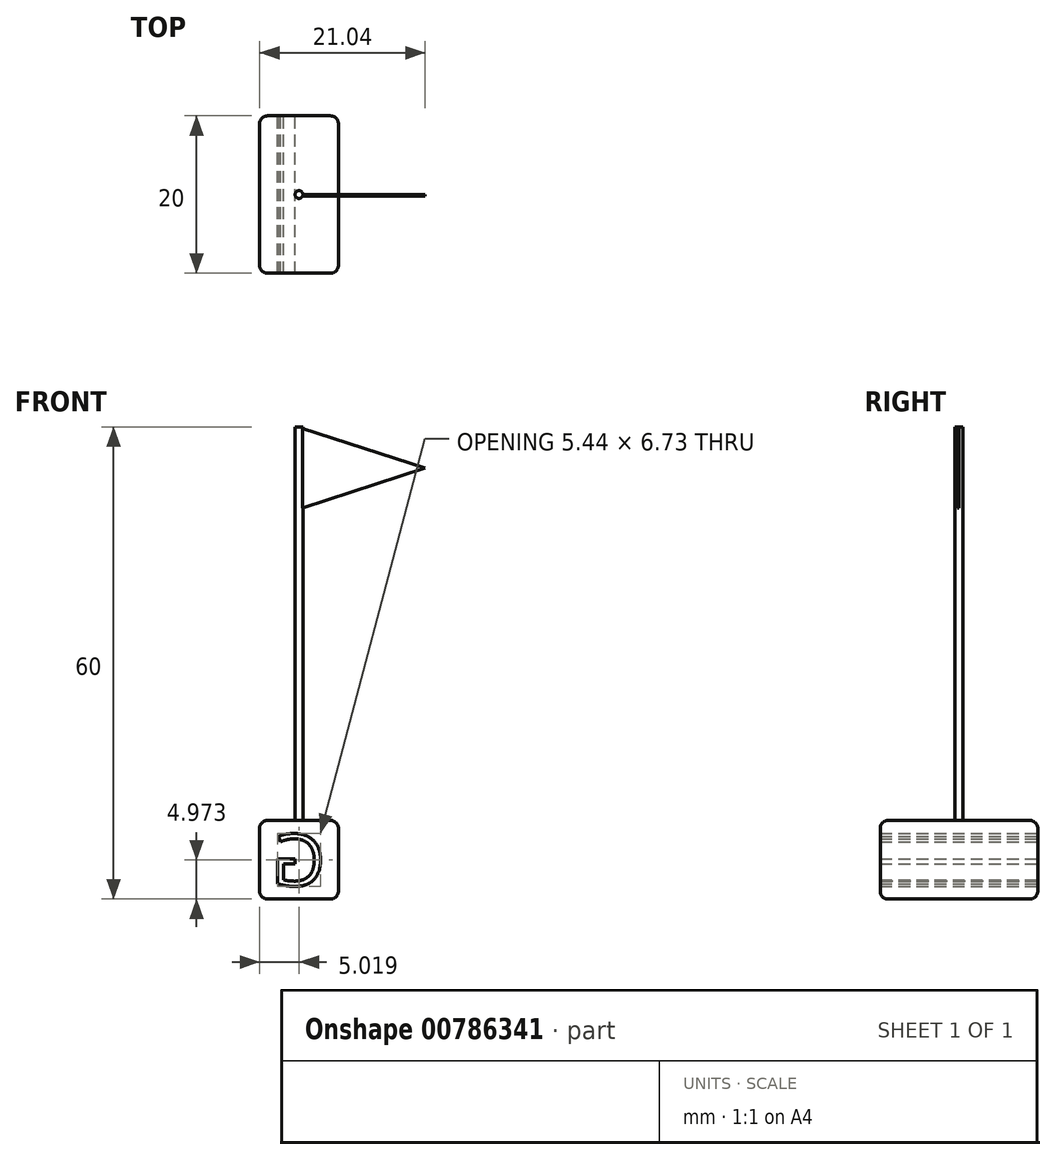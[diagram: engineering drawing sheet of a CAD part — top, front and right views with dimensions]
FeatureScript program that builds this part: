
annotation { "Feature Type Name" : "Feature", "Feature Type Description" : "" }
export const myFeature = defineFeature(function(context is Context, id is Id, definition is map)
    precondition{}
    {
        {
            var Q0;
            Q0=qCreatedBy(makeId("Front.planeOp"),FACE);
            var sketch = newSketch(context, id + "F0", { "sketchPlane" : qUnion([Q0])});
            skLineSegment(sketch, "E0.bottom", {"start": v(0, 0) * mm, "end": v(10, 0) * mm});
            skLineSegment(sketch, "E0.top", {"start": v(0, 10) * mm, "end": v(10, 10) * mm});
            skLineSegment(sketch, "E0.left", {"start": v(0, 0) * mm, "end": v(0, 10) * mm});
            skLineSegment(sketch, "E0.right", {"start": v(10, 0) * mm, "end": v(10, 10) * mm});
            skSolve(sketch);
        }
        {
            var Q0;
            Q0 = qSketchRegion(id + "F0", true);
            extrude(context, id + "F1", {"entities" : qUnion([Q0]), "depth" : 20 * mm, "offsetDistance" : 25 * mm});
        }
        {
            var Q0;
            Q0=makeQuery(id+"F1.opExtrude","CAP_FACE",FACE,{"disambiguationData":[OSD([sQuery(id+"F0.wireOp",EDGE,"E0.bottom"),sQuery(id+"F0.wireOp",EDGE,"E0.top"),sQuery(id+"F0.wireOp",EDGE,"E0.left"),sQuery(id+"F0.wireOp",EDGE,"E0.right")])],"isStart":false});
            var Q1;
            Q1=makeQuery(id+"F1.opExtrude","SWEPT_FACE",FACE,{"disambiguationData":[OSD([sQuery(id+"F0.wireOp",EDGE,"E0.right")])]});
            var Q2;
            Q2=makeQuery(id+"F1.opExtrude","CAP_FACE",FACE,{"disambiguationData":[OSD([sQuery(id+"F0.wireOp",EDGE,"E0.bottom"),sQuery(id+"F0.wireOp",EDGE,"E0.top"),sQuery(id+"F0.wireOp",EDGE,"E0.left"),sQuery(id+"F0.wireOp",EDGE,"E0.right")])],"isStart":true});
            var Q3;
            Q3=makeQuery(id+"F1.opExtrude","SWEPT_FACE",FACE,{"disambiguationData":[OSD([sQuery(id+"F0.wireOp",EDGE,"E0.left")])]});
            fillet(context, id + "F2", {"entities" : qUnion([Q0, Q1, Q2, Q3]), "radius" : 1 * mm, "tangentPropagation" : true, "allowEdgeOverflow" : false});
        }
        {
            var Q0;
            Q0=makeQuery(id+"F1.opExtrude","SWEPT_FACE",FACE,{"disambiguationData":[OSD([sQuery(id+"F0.wireOp",EDGE,"E0.top")])]});
            var sketch = newSketch(context, id + "F3", { "sketchPlane" : qUnion([Q0])});
            skLineSegment(sketch, "E1", {"start": v(5, -1) * mm, "end": v(5, -19) * mm, "construction": true});
            skCircle(sketch, "E2", {"center": v(5, -10) * mm, "radius": 0.5 * mm});
            skSolve(sketch);
        }
        {
            var Q0;
            Q0 = qSketchRegion(id + "F3", true);
            extrude(context, id + "F4", {"entities" : qUnion([Q0]), "operationType" : NewBodyOperationType.ADD, "depth" : 50 * mm, "offsetDistance" : 25 * mm});
        }
        {
            var Q0;
            Q0=qCreatedBy(makeId("Front.planeOp"),FACE);
            cPlane(context, id + "F5", {"entities" : qUnion([Q0]), "cplaneType" : CPlaneType.OFFSET, "offset" : 10 * mm, "width" : 150 * mm, "height" : 150 * mm});
        }
        {
            var Q0;
            Q0=qCreatedBy(id+"F5.planeOp",FACE);
            var sketch = newSketch(context, id + "F6", { "sketchPlane" : qUnion([Q0])});
            skLineSegment(sketch, "E3", {"start": v(4.88, 59.98) * mm, "end": v(21.04, 54.77) * mm});
            skLineSegment(sketch, "E4", {"start": v(21.04, 54.77) * mm, "end": v(5, 49.51) * mm});
            skLineSegment(sketch, "E5", {"start": v(5, 49.51) * mm, "end": v(4.88, 59.98) * mm});
            skSolve(sketch);
        }
        {
            var Q0;
            Q0 = qSketchRegion(id + "F6", true);
            extrude(context, id + "F7", {"entities" : qUnion([Q0]), "operationType" : NewBodyOperationType.ADD, "depth" : 0.2 * mm, "offsetDistance" : 25 * mm});
        }
        {
            var Q0;
            Q0=makeQuery(id+"F1.opExtrude","CAP_FACE",FACE,{"disambiguationData":[OSD([sQuery(id+"F0.wireOp",EDGE,"E0.bottom"),sQuery(id+"F0.wireOp",EDGE,"E0.top"),sQuery(id+"F0.wireOp",EDGE,"E0.left"),sQuery(id+"F0.wireOp",EDGE,"E0.right")])],"isStart":true});
            var sketch = newSketch(context, id + "F8", { "sketchPlane" : qUnion([Q0])});
            skText(sketch, "E6", { "text": "G\n", "fontName": "OpenSans-Regular.ttf"});
            const initialGuessF8  = {"E6": [-0.0083, 0.0017, 1, 0, 0.0066]};
            skSetInitialGuess(sketch, initialGuessF8);
            skSolve(sketch);
        }
        {
            var Q0;
            Q0 = qSketchRegion(id + "F8", true);
            extrude(context, id + "F9", {"entities" : qUnion([Q0]), "operationType" : NewBodyOperationType.REMOVE, "oppositeDirection" : true, "depth" : 30 * mm, "offsetDistance" : 25 * mm});
        }
    });
